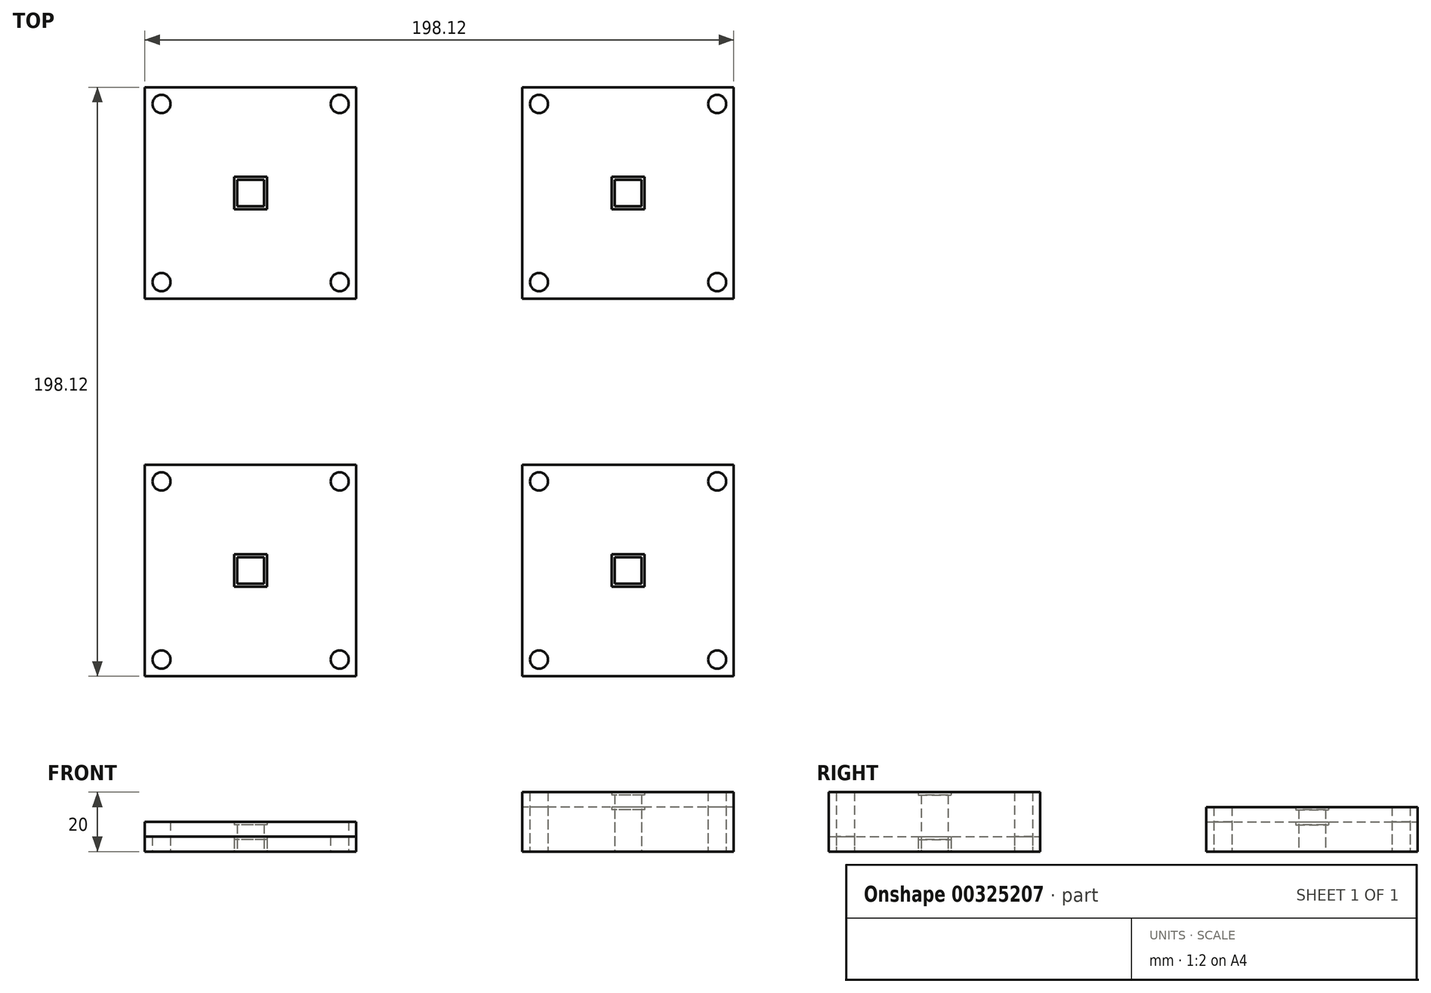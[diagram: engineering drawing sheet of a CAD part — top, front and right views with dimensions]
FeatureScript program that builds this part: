
annotation { "Feature Type Name" : "Feature", "Feature Type Description" : "" }
export const myFeature = defineFeature(function(context is Context, id is Id, definition is map)
    precondition{}
    {
        {
            var Q0;
            Q0=qCreatedBy(makeId("Top.planeOp"),FACE);
            var sketch = newSketch(context, id + "F0", { "sketchPlane" : qUnion([Q0])});
            skLineSegment(sketch, "E0.bottom", {"start": v(35.56, -35.56) * mm, "end": v(-35.56, -35.56) * mm});
            skLineSegment(sketch, "E0.top", {"start": v(35.56, 35.56) * mm, "end": v(-35.56, 35.56) * mm});
            skLineSegment(sketch, "E0.left", {"start": v(35.56, -35.56) * mm, "end": v(35.56, 35.56) * mm});
            skLineSegment(sketch, "E0.right", {"start": v(-35.56, -35.56) * mm, "end": v(-35.56, 35.56) * mm});
            skPoint(sketch, "E0.middle", {"position": v(0, 0) * mm});
            skLineSegment(sketch, "E1.bottom", {"start": v(4.5, 4.5) * mm, "end": v(-4.5, 4.5) * mm});
            skLineSegment(sketch, "E1.top", {"start": v(4.5, -4.5) * mm, "end": v(-4.5, -4.5) * mm});
            skLineSegment(sketch, "E1.left", {"start": v(4.5, 4.5) * mm, "end": v(4.5, -4.5) * mm});
            skLineSegment(sketch, "E1.right", {"start": v(-4.5, 4.5) * mm, "end": v(-4.5, -4.5) * mm});
            skCircle(sketch, "E2", {"center": v(-29.97, 29.97) * mm, "radius": 3.05 * mm});
            skCircle(sketch, "E3", {"center": v(29.97, 29.97) * mm, "radius": 3.05 * mm});
            skCircle(sketch, "E4", {"center": v(-29.97, -29.97) * mm, "radius": 3.05 * mm});
            skCircle(sketch, "E5", {"center": v(29.97, -29.97) * mm, "radius": 3.05 * mm});
            skLineSegment(sketch, "E6.0.1.0", {"start": v(35.56, 91.44) * mm, "end": v(-35.56, 91.44) * mm});
            skLineSegment(sketch, "E6.0.1.1", {"start": v(4.5, 131.5) * mm, "end": v(4.5, 122.5) * mm});
            skCircle(sketch, "E6.0.1.2", {"center": v(-29.97, 97.03) * mm, "radius": 3.05 * mm});
            skPoint(sketch, "E6.0.1.3", {"position": v(0, 127) * mm});
            skLineSegment(sketch, "E6.0.1.4", {"start": v(-35.56, 91.44) * mm, "end": v(-35.56, 162.56) * mm});
            skLineSegment(sketch, "E6.0.1.5", {"start": v(35.56, 91.44) * mm, "end": v(35.56, 162.56) * mm});
            skLineSegment(sketch, "E6.0.1.6", {"start": v(35.56, 162.56) * mm, "end": v(-35.56, 162.56) * mm});
            skCircle(sketch, "E6.0.1.7", {"center": v(-29.97, 156.97) * mm, "radius": 3.05 * mm});
            skPoint(sketch, "E6.0.1.8", {"position": v(0, 127) * mm});
            skCircle(sketch, "E6.0.1.9", {"center": v(29.97, 156.97) * mm, "radius": 3.05 * mm});
            skLineSegment(sketch, "E6.0.1.10", {"start": v(4.5, 131.5) * mm, "end": v(-4.5, 131.5) * mm});
            skCircle(sketch, "E6.0.1.11", {"center": v(29.97, 97.03) * mm, "radius": 3.05 * mm});
            skLineSegment(sketch, "E6.0.1.12", {"start": v(4.5, 122.5) * mm, "end": v(-4.5, 122.5) * mm});
            skLineSegment(sketch, "E6.0.1.13", {"start": v(-4.5, 131.5) * mm, "end": v(-4.5, 122.5) * mm});
            skLineSegment(sketch, "E6.1.0.0", {"start": v(162.56, -35.56) * mm, "end": v(91.44, -35.56) * mm});
            skLineSegment(sketch, "E6.1.0.1", {"start": v(131.5, 4.5) * mm, "end": v(131.5, -4.5) * mm});
            skCircle(sketch, "E6.1.0.2", {"center": v(97.03, -29.97) * mm, "radius": 3.05 * mm});
            skPoint(sketch, "E6.1.0.3", {"position": v(127, 0) * mm});
            skLineSegment(sketch, "E6.1.0.4", {"start": v(91.44, -35.56) * mm, "end": v(91.44, 35.56) * mm});
            skLineSegment(sketch, "E6.1.0.5", {"start": v(162.56, -35.56) * mm, "end": v(162.56, 35.56) * mm});
            skLineSegment(sketch, "E6.1.0.6", {"start": v(162.56, 35.56) * mm, "end": v(91.44, 35.56) * mm});
            skCircle(sketch, "E6.1.0.7", {"center": v(97.03, 29.97) * mm, "radius": 3.05 * mm});
            skPoint(sketch, "E6.1.0.8", {"position": v(127, 0) * mm});
            skCircle(sketch, "E6.1.0.9", {"center": v(156.97, 29.97) * mm, "radius": 3.05 * mm});
            skLineSegment(sketch, "E6.1.0.10", {"start": v(131.5, 4.5) * mm, "end": v(122.5, 4.5) * mm});
            skCircle(sketch, "E6.1.0.11", {"center": v(156.97, -29.97) * mm, "radius": 3.05 * mm});
            skLineSegment(sketch, "E6.1.0.12", {"start": v(131.5, -4.5) * mm, "end": v(122.5, -4.5) * mm});
            skLineSegment(sketch, "E6.1.0.13", {"start": v(122.5, 4.5) * mm, "end": v(122.5, -4.5) * mm});
            skLineSegment(sketch, "E6.1.1.0", {"start": v(162.56, 91.44) * mm, "end": v(91.44, 91.44) * mm});
            skLineSegment(sketch, "E6.1.1.1", {"start": v(131.5, 131.5) * mm, "end": v(131.5, 122.5) * mm});
            skCircle(sketch, "E6.1.1.2", {"center": v(97.03, 97.03) * mm, "radius": 3.05 * mm});
            skPoint(sketch, "E6.1.1.3", {"position": v(127, 127) * mm});
            skLineSegment(sketch, "E6.1.1.4", {"start": v(91.44, 91.44) * mm, "end": v(91.44, 162.56) * mm});
            skLineSegment(sketch, "E6.1.1.5", {"start": v(162.56, 91.44) * mm, "end": v(162.56, 162.56) * mm});
            skLineSegment(sketch, "E6.1.1.6", {"start": v(162.56, 162.56) * mm, "end": v(91.44, 162.56) * mm});
            skCircle(sketch, "E6.1.1.7", {"center": v(97.03, 156.97) * mm, "radius": 3.05 * mm});
            skPoint(sketch, "E6.1.1.8", {"position": v(127, 127) * mm});
            skCircle(sketch, "E6.1.1.9", {"center": v(156.97, 156.97) * mm, "radius": 3.05 * mm});
            skLineSegment(sketch, "E6.1.1.10", {"start": v(131.5, 131.5) * mm, "end": v(122.5, 131.5) * mm});
            skCircle(sketch, "E6.1.1.11", {"center": v(156.97, 97.03) * mm, "radius": 3.05 * mm});
            skLineSegment(sketch, "E6.1.1.12", {"start": v(131.5, 122.5) * mm, "end": v(122.5, 122.5) * mm});
            skLineSegment(sketch, "E6.1.1.13", {"start": v(122.5, 131.5) * mm, "end": v(122.5, 122.5) * mm});
            skLineSegment(sketch, "E6.direction1", {"start": v(-35.56, -35.56) * mm, "end": v(91.44, -35.56) * mm, "construction": true});
            skLineSegment(sketch, "E6.direction2", {"start": v(-35.56, -35.56) * mm, "end": v(-35.56, 91.44) * mm, "construction": true});
            skLineSegment(sketch, "E7.bottom", {"start": v(5.5, -5.5) * mm, "end": v(-5.5, -5.5) * mm});
            skLineSegment(sketch, "E7.top", {"start": v(5.5, 5.5) * mm, "end": v(-5.5, 5.5) * mm});
            skLineSegment(sketch, "E7.left", {"start": v(5.5, -5.5) * mm, "end": v(5.5, 5.5) * mm});
            skLineSegment(sketch, "E7.right", {"start": v(-5.5, -5.5) * mm, "end": v(-5.5, 5.5) * mm});
            skLineSegment(sketch, "E8.bottom", {"start": v(5.5, 121.5) * mm, "end": v(-5.5, 121.5) * mm});
            skLineSegment(sketch, "E8.top", {"start": v(5.5, 132.5) * mm, "end": v(-5.5, 132.5) * mm});
            skLineSegment(sketch, "E8.left", {"start": v(5.5, 121.5) * mm, "end": v(5.5, 132.5) * mm});
            skLineSegment(sketch, "E8.right", {"start": v(-5.5, 121.5) * mm, "end": v(-5.5, 132.5) * mm});
            skLineSegment(sketch, "E9.bottom", {"start": v(132.5, 121.5) * mm, "end": v(121.5, 121.5) * mm});
            skLineSegment(sketch, "E9.top", {"start": v(132.5, 132.5) * mm, "end": v(121.5, 132.5) * mm});
            skLineSegment(sketch, "E9.left", {"start": v(132.5, 121.5) * mm, "end": v(132.5, 132.5) * mm});
            skLineSegment(sketch, "E9.right", {"start": v(121.5, 121.5) * mm, "end": v(121.5, 132.5) * mm});
            skLineSegment(sketch, "E10.bottom", {"start": v(132.5, -5.5) * mm, "end": v(121.5, -5.5) * mm});
            skLineSegment(sketch, "E10.top", {"start": v(132.5, 5.5) * mm, "end": v(121.5, 5.5) * mm});
            skLineSegment(sketch, "E10.left", {"start": v(132.5, -5.5) * mm, "end": v(132.5, 5.5) * mm});
            skLineSegment(sketch, "E10.right", {"start": v(121.5, -5.5) * mm, "end": v(121.5, 5.5) * mm});
            skSolve(sketch);
        }
        {
            var Q0;
            Q0=makeQuery(id+"F0.imprint","IMPRINT",FACE,{"disambiguationData":[TD([[makeQuery(id+"F0.imprint","IMPRINT",EDGE,{"derivedFrom":sQuery(id+"F0.wireOp",EDGE,"E0.bottom")}),-1.0]])]});
            extrude(context, id + "F1", {"entities" : qUnion([Q0]), "depth" : 5 * mm});
        }
        {
            var Q0;
            Q0=makeQuery(id+"F0.imprint","IMPRINT",FACE,{"disambiguationData":[TD([[makeQuery(id+"F0.imprint","IMPRINT",EDGE,{"derivedFrom":sQuery(id+"F0.wireOp",EDGE,"E6.0.1.0")}),-1.0]])]});
            extrude(context, id + "F2", {"entities" : qUnion([Q0]), "operationType" : NewBodyOperationType.ADD, "depth" : 10 * mm});
        }
        {
            var Q0;
            Q0=makeQuery(id+"F0.imprint","IMPRINT",FACE,{"disambiguationData":[TD([[makeQuery(id+"F0.imprint","IMPRINT",EDGE,{"derivedFrom":sQuery(id+"F0.wireOp",EDGE,"E6.1.1.0")}),-1.0]])]});
            extrude(context, id + "F3", {"entities" : qUnion([Q0]), "depth" : 15 * mm});
        }
        {
            var Q0;
            Q0=makeQuery(id+"F0.imprint","IMPRINT",FACE,{"disambiguationData":[TD([[makeQuery(id+"F0.imprint","IMPRINT",EDGE,{"derivedFrom":sQuery(id+"F0.wireOp",EDGE,"E6.1.0.0")}),-1.0]])]});
            extrude(context, id + "F4", {"entities" : qUnion([Q0]), "depth" : 20 * mm});
        }
        {
            var Q0;
            Q0=makeQuery(id+"F0.imprint","IMPRINT",FACE,{"disambiguationData":[TD([[makeQuery(id+"F0.imprint","IMPRINT",EDGE,{"derivedFrom":sQuery(id+"F0.wireOp",EDGE,"E1.bottom")}),-1.0]])]});
            extrude(context, id + "F5", {"entities" : qUnion([Q0]), "depth" : 4 * mm});
        }
        {
            var Q0;
            Q0=makeQuery(id+"F0.imprint","IMPRINT",FACE,{"disambiguationData":[TD([[makeQuery(id+"F0.imprint","IMPRINT",EDGE,{"derivedFrom":sQuery(id+"F0.wireOp",EDGE,"E6.0.1.1")}),1.0]])]});
            extrude(context, id + "F6", {"entities" : qUnion([Q0]), "operationType" : NewBodyOperationType.ADD, "depth" : 9 * mm});
        }
        {
            var Q0;
            Q0=makeQuery(id+"F0.imprint","IMPRINT",FACE,{"disambiguationData":[TD([[makeQuery(id+"F0.imprint","IMPRINT",EDGE,{"derivedFrom":sQuery(id+"F0.wireOp",EDGE,"E6.1.1.1")}),1.0]])]});
            extrude(context, id + "F7", {"entities" : qUnion([Q0]), "operationType" : NewBodyOperationType.ADD, "depth" : 14 * mm});
        }
        {
            var Q0;
            Q0=makeQuery(id+"F0.imprint","IMPRINT",FACE,{"disambiguationData":[TD([[makeQuery(id+"F0.imprint","IMPRINT",EDGE,{"derivedFrom":sQuery(id+"F0.wireOp",EDGE,"E6.1.0.1")}),1.0]])]});
            extrude(context, id + "F8", {"entities" : qUnion([Q0]), "operationType" : NewBodyOperationType.ADD, "depth" : 19 * mm});
        }
    });
